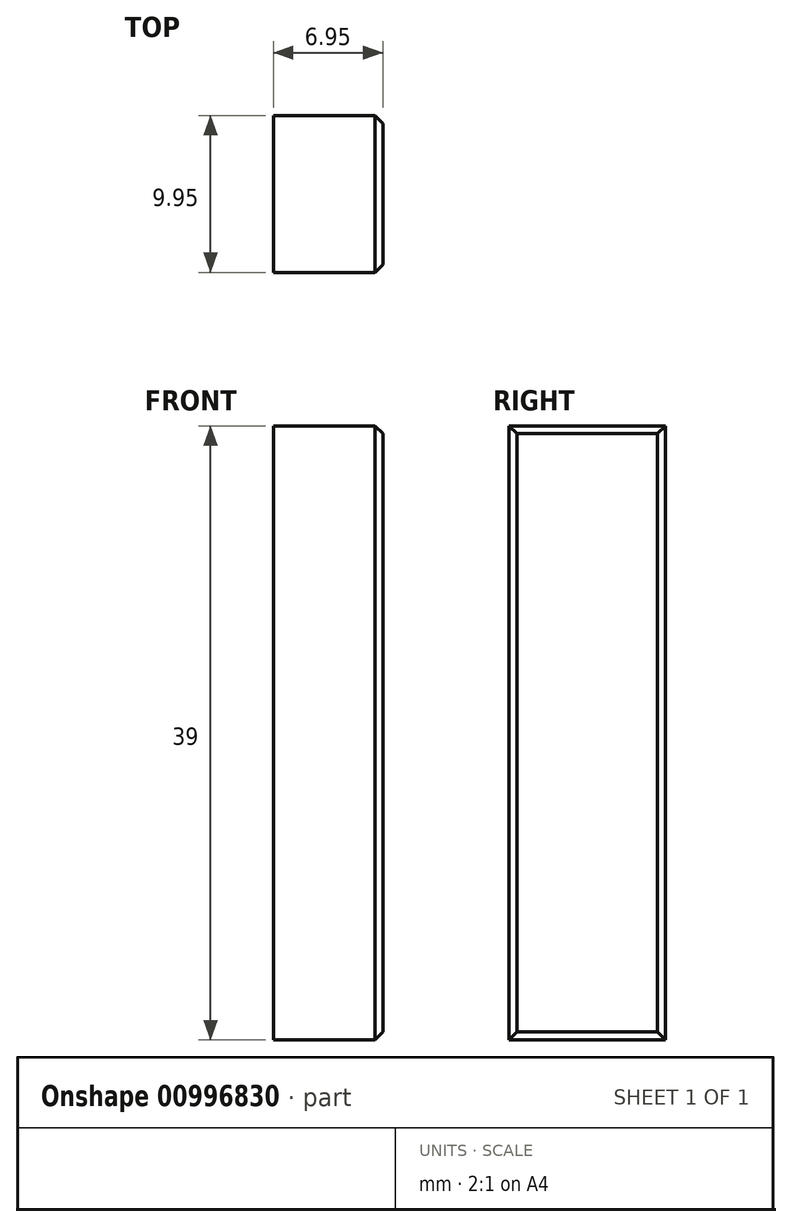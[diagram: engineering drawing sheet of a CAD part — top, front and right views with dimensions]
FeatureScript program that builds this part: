
annotation { "Feature Type Name" : "Feature", "Feature Type Description" : "" }
export const myFeature = defineFeature(function(context is Context, id is Id, definition is map)
    precondition{}
    {
        {
            var Q0;
            Q0=qCreatedBy(makeId("Top.planeOp"),FACE);
            var sketch = newSketch(context, id + "F0", { "sketchPlane" : qUnion([Q0])});
            skLineSegment(sketch, "E0.bottom", {"start": v(0, 0) * mm, "end": v(6.95, 0) * mm});
            skLineSegment(sketch, "E0.top", {"start": v(0, 9.95) * mm, "end": v(6.95, 9.95) * mm});
            skLineSegment(sketch, "E0.left", {"start": v(0, 0) * mm, "end": v(0, 9.95) * mm});
            skLineSegment(sketch, "E0.right", {"start": v(6.95, 0) * mm, "end": v(6.95, 9.95) * mm});
            skSolve(sketch);
        }
        {
            var Q0;
            Q0 = qSketchRegion(id + "F0", true);
            extrude(context, id + "F1", {"entities" : qUnion([Q0]), "depth" : 39 * mm, "offsetDistance" : 25 * mm});
        }
        {
            var Q0;
            Q0=makeQuery(id+"F1.opExtrude","SWEPT_EDGE",EDGE,{"disambiguationData":[OSD([sQuery(id+"F0.wireOp",EDGE,"E0.top"),sQuery(id+"F0.wireOp",EDGE,"E0.right")])]});
            var Q1;
            Q1=makeQuery(id+"F1.opExtrude","SWEPT_EDGE",EDGE,{"disambiguationData":[OSD([sQuery(id+"F0.wireOp",EDGE,"E0.bottom"),sQuery(id+"F0.wireOp",EDGE,"E0.right")])]});
            var Q2;
            Q2=makeQuery(id+"F1.opExtrude","CAP_EDGE",EDGE,{"disambiguationData":[OSD([sQuery(id+"F0.wireOp",EDGE,"E0.right")])],"isStart":false});
            var Q3;
            Q3=makeQuery(id+"F1.opExtrude","CAP_EDGE",EDGE,{"disambiguationData":[OSD([sQuery(id+"F0.wireOp",EDGE,"E0.right")])],"isStart":true});
            chamfer(context, id + "F2", {"entities" : qUnion([Q0, Q1, Q2, Q3]), "width" : 0.5 * mm, "tangentPropagation" : true});
        }
    });
